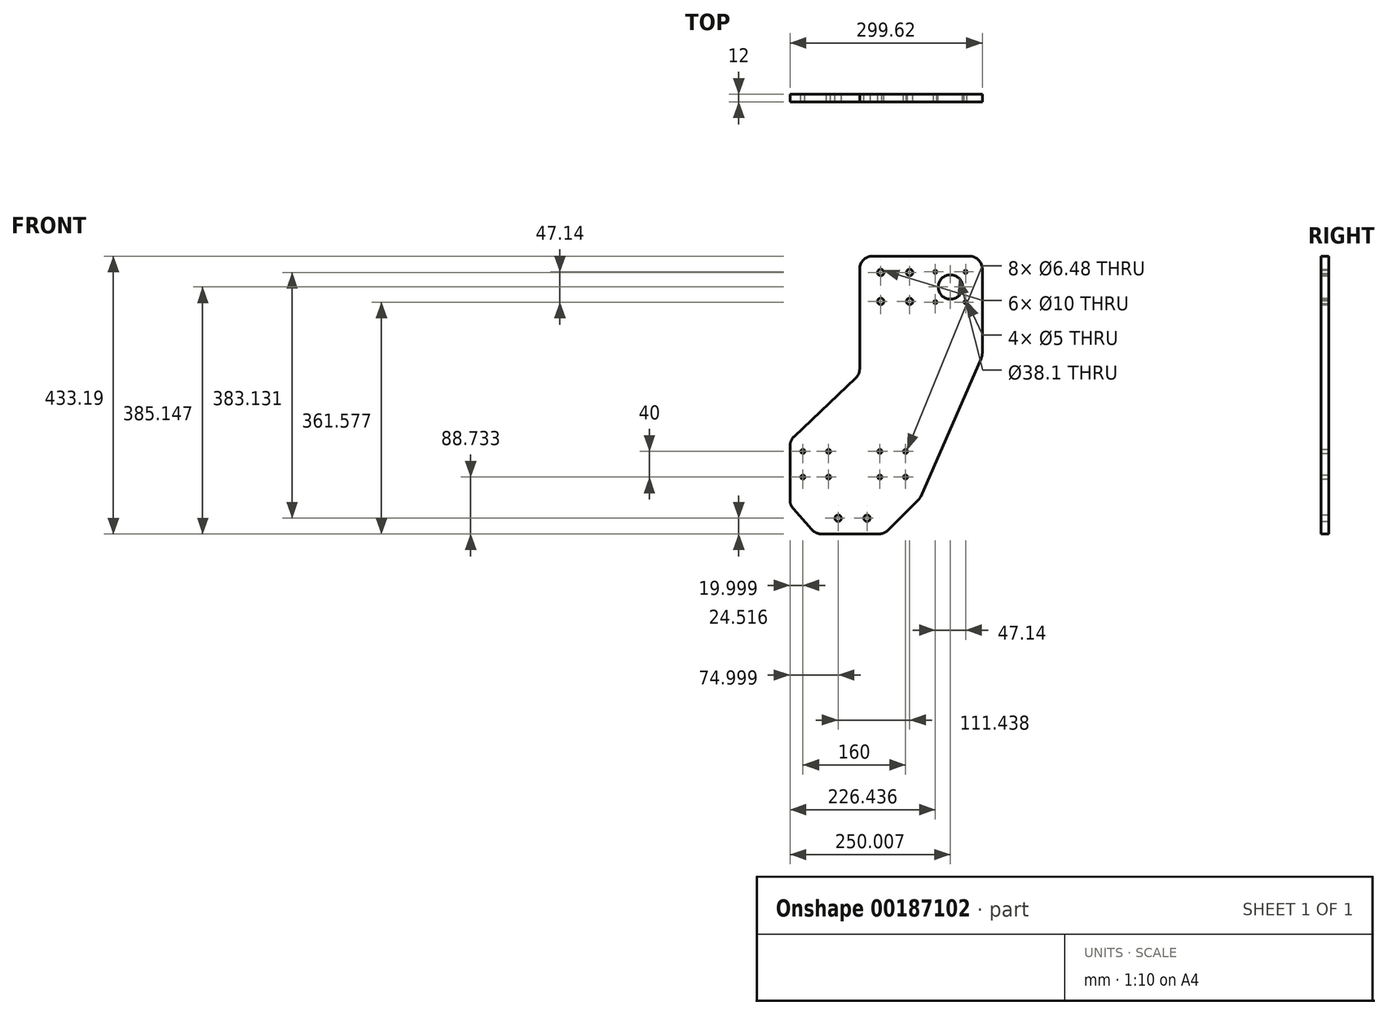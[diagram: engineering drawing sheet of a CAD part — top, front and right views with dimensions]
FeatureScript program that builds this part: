
annotation { "Feature Type Name" : "Feature", "Feature Type Description" : "" }
export const myFeature = defineFeature(function(context is Context, id is Id, definition is map)
    precondition{}
    {
        {
            var Q0;
            Q0=qCreatedBy(makeId("Front.planeOp"),FACE);
            var sketch = newSketch(context, id + "F0", { "sketchPlane" : qUnion([Q0])});
            skPoint(sketch, "E0.middle", {"position": v(0, 0) * mm});
            skCircle(sketch, "E1", {"center": v(-73.34, -139.46) * mm, "radius": 3.24 * mm});
            skCircle(sketch, "E2", {"center": v(-73.34, -99.46) * mm, "radius": 3.24 * mm});
            skCircle(sketch, "E3", {"center": v(-33.34, -99.46) * mm, "radius": 3.24 * mm});
            skCircle(sketch, "E4", {"center": v(-33.34, -139.46) * mm, "radius": 3.24 * mm});
            skCircle(sketch, "E5", {"center": v(46.66, -99.46) * mm, "radius": 3.24 * mm});
            skCircle(sketch, "E6", {"center": v(46.66, -139.46) * mm, "radius": 3.24 * mm});
            skCircle(sketch, "E7", {"center": v(86.66, -139.46) * mm, "radius": 3.24 * mm});
            skCircle(sketch, "E8", {"center": v(86.66, -99.46) * mm, "radius": 3.24 * mm});
            skCircle(sketch, "E9", {"center": v(-18.34, -203.67) * mm, "radius": 5 * mm});
            skCircle(sketch, "E10", {"center": v(26.66, -203.67) * mm, "radius": 5 * mm});
            skCircle(sketch, "E11", {"center": v(48.1, 179.46) * mm, "radius": 5 * mm});
            skCircle(sketch, "E12", {"center": v(93.1, 179.46) * mm, "radius": 5 * mm});
            skCircle(sketch, "E13", {"center": v(48.1, 134.46) * mm, "radius": 5 * mm});
            skCircle(sketch, "E14", {"center": v(93.1, 134.46) * mm, "radius": 5 * mm});
            skCircle(sketch, "E15", {"center": v(133.1, 180.53) * mm, "radius": 2.5 * mm});
            skCircle(sketch, "E16", {"center": v(180.24, 180.53) * mm, "radius": 2.5 * mm});
            skCircle(sketch, "E17", {"center": v(133.1, 133.39) * mm, "radius": 2.5 * mm});
            skCircle(sketch, "E18", {"center": v(180.24, 133.39) * mm, "radius": 2.5 * mm});
            skCircle(sketch, "E19", {"center": v(156.67, 156.96) * mm, "radius": 19.05 * mm});
            skLineSegment(sketch, "E20", {"start": v(-93.34, -135.08) * mm, "end": v(-93.34, -175.45) * mm});
            skLineSegment(sketch, "E21", {"start": v(115.36, 205) * mm, "end": v(173.13, 205) * mm});
            skLineSegment(sketch, "E22", {"start": v(-44.3, -228.2) * mm, "end": v(45.14, -228.2) * mm});
            skLineSegment(sketch, "E23", {"start": v(-88.3, -188.72) * mm, "end": v(-59.26, -221.46) * mm});
            skLineSegment(sketch, "E24", {"start": v(59.24, -222.38) * mm, "end": v(106.27, -175.65) * mm});
            skPoint(sketch, "E25.visualSharp", {"position": v(53.4, -228.2) * mm});
            skArc(sketch, "E25.filletArc", {"start": v(45.14, -228.2) * mm, "mid": v(52.77, -226.68) * mm, "end": v(59.24, -222.38) * mm});
            skPoint(sketch, "E26.visualSharp", {"position": v(-53.29, -228.2) * mm});
            skArc(sketch, "E26.filletArc", {"start": v(-59.26, -221.46) * mm, "mid": v(-52.5, -226.43) * mm, "end": v(-44.3, -228.2) * mm});
            skPoint(sketch, "E27.visualSharp", {"position": v(-93.34, -183.04) * mm});
            skArc(sketch, "E27.filletArc", {"start": v(-93.34, -175.45) * mm, "mid": v(-92.04, -182.55) * mm, "end": v(-88.3, -188.72) * mm});
            skLineSegment(sketch, "E28", {"start": v(173.13, 205) * mm, "end": v(186.28, 205) * mm});
            skLineSegment(sketch, "E29", {"start": v(206.28, 185) * mm, "end": v(206.28, 53.25) * mm});
            skPoint(sketch, "E30.visualSharp", {"position": v(206.28, 205) * mm});
            skArc(sketch, "E30.filletArc", {"start": v(206.28, 185) * mm, "mid": v(200.42, 199.14) * mm, "end": v(186.28, 205) * mm});
            skLineSegment(sketch, "E31", {"start": v(204.6, 45.23) * mm, "end": v(110.49, -169.5) * mm});
            skPoint(sketch, "E32.visualSharp", {"position": v(206.28, 49.06) * mm});
            skArc(sketch, "E32.filletArc", {"start": v(204.6, 45.23) * mm, "mid": v(205.85, 49.15) * mm, "end": v(206.28, 53.25) * mm});
            skPoint(sketch, "E33.visualSharp", {"position": v(108.96, -172.97) * mm});
            skArc(sketch, "E33.filletArc", {"start": v(106.27, -175.65) * mm, "mid": v(108.67, -172.77) * mm, "end": v(110.49, -169.5) * mm});
            skLineSegment(sketch, "E34", {"start": v(115.36, 205) * mm, "end": v(35.19, 205) * mm});
            skLineSegment(sketch, "E35", {"start": v(15.19, 185) * mm, "end": v(15.19, 29.44) * mm});
            skPoint(sketch, "E36.visualSharp", {"position": v(15.19, 205) * mm});
            skArc(sketch, "E36.filletArc", {"start": v(35.19, 205) * mm, "mid": v(21.05, 199.14) * mm, "end": v(15.19, 185) * mm});
            skLineSegment(sketch, "E37", {"start": v(-93.34, -135.08) * mm, "end": v(-93.34, -90.77) * mm});
            skLineSegment(sketch, "E38", {"start": v(-87.11, -76.27) * mm, "end": v(8.96, 14.93) * mm});
            skPoint(sketch, "E39.visualSharp", {"position": v(15.19, 20.85) * mm});
            skArc(sketch, "E39.filletArc", {"start": v(8.96, 14.93) * mm, "mid": v(13.57, 21.55) * mm, "end": v(15.19, 29.44) * mm});
            skPoint(sketch, "E40.visualSharp", {"position": v(-93.34, -82.18) * mm});
            skArc(sketch, "E40.filletArc", {"start": v(-87.11, -76.27) * mm, "mid": v(-91.72, -82.88) * mm, "end": v(-93.34, -90.77) * mm});
            skSolve(sketch);
        }
        {
            var Q0;
            Q0=makeQuery(id+"F0.imprint","IMPRINT",FACE,{"disambiguationData":[TD([[makeQuery(id+"F0.imprint","IMPRINT",EDGE,{"derivedFrom":sQuery(id+"F0.wireOp",EDGE,"E1")}),-1.0]])]});
            extrude(context, id + "F1", {"entities" : qUnion([Q0]), "depth" : 12 * mm});
        }
    });
